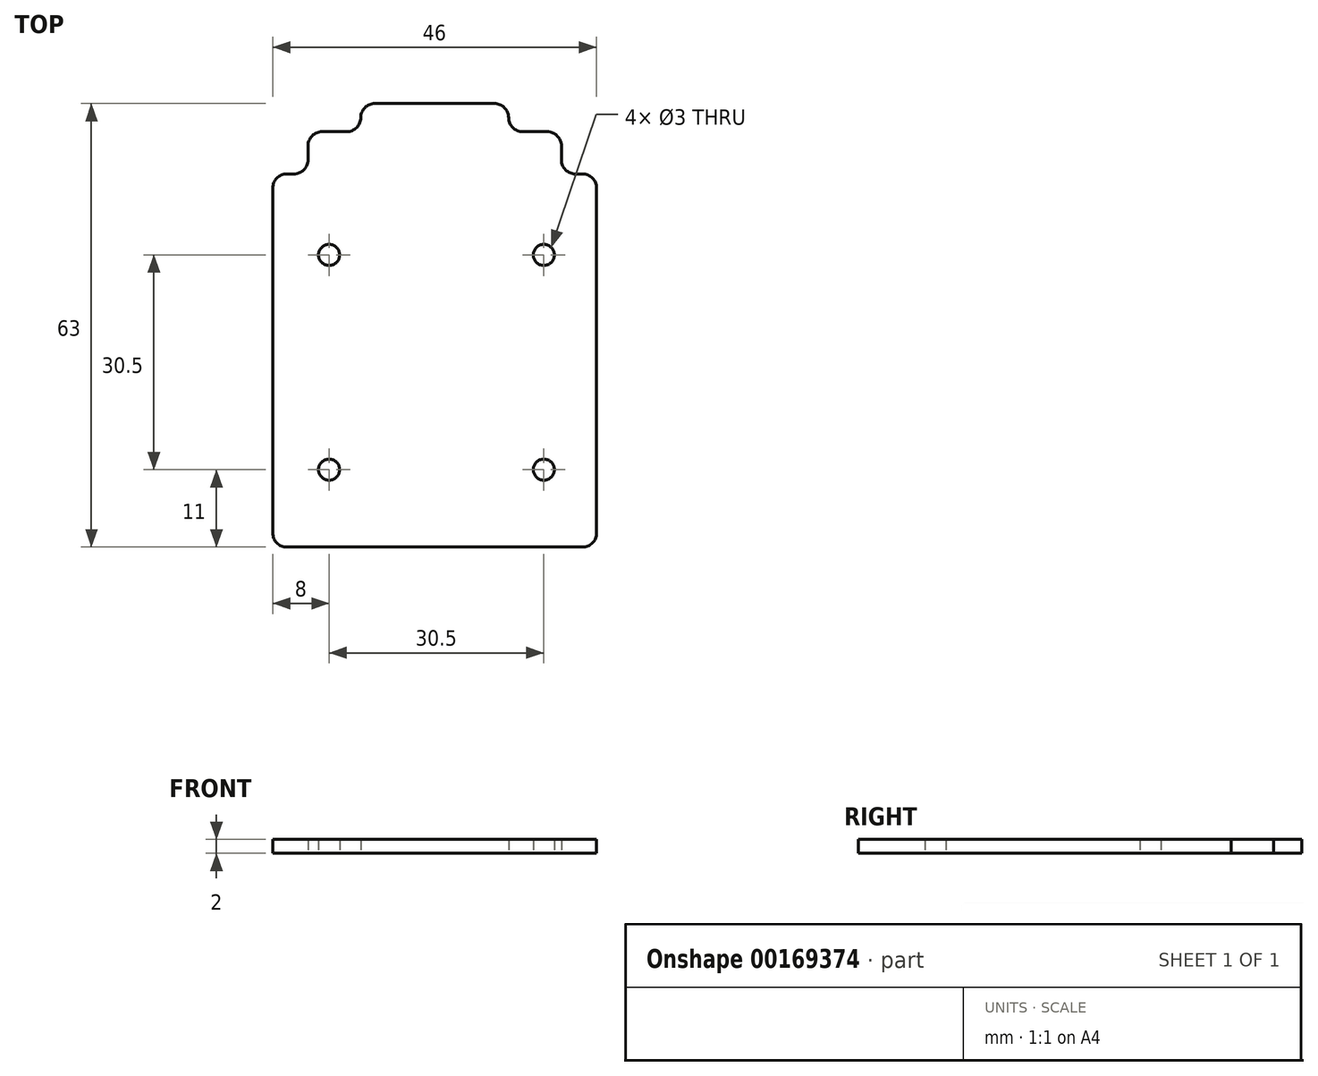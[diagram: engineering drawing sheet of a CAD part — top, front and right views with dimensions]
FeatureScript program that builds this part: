
annotation { "Feature Type Name" : "Feature", "Feature Type Description" : "" }
export const myFeature = defineFeature(function(context is Context, id is Id, definition is map)
    precondition{}
    {
        {
            var Q0;
            Q0=qCreatedBy(makeId("Top.planeOp"),FACE);
            var sketch = newSketch(context, id + "F0", { "sketchPlane" : qUnion([Q0])});
            skLineSegment(sketch, "E0.bottom", {"start": v(-10.5, 31.5) * mm, "end": v(10.5, 31.5) * mm});
            skLineSegment(sketch, "E0.top", {"start": v(-23, -31.5) * mm, "end": v(23, -31.5) * mm});
            skLineSegment(sketch, "E0.left", {"start": v(-23, 21.5) * mm, "end": v(-23, -31.5) * mm});
            skLineSegment(sketch, "E0.right", {"start": v(23, 21.5) * mm, "end": v(23, -31.5) * mm});
            skCircle(sketch, "E1", {"center": v(-15, -20.5) * mm, "radius": 1.5 * mm});
            skCircle(sketch, "E2.0.1.0", {"center": v(-15, 10) * mm, "radius": 1.5 * mm});
            skCircle(sketch, "E2.1.0.0", {"center": v(15.5, -20.5) * mm, "radius": 1.5 * mm});
            skCircle(sketch, "E2.1.1.0", {"center": v(15.5, 10) * mm, "radius": 1.5 * mm});
            skLineSegment(sketch, "E2.direction1", {"start": v(-15, -20.5) * mm, "end": v(15.5, -20.5) * mm, "construction": true});
            skLineSegment(sketch, "E2.direction2", {"start": v(-15, -20.5) * mm, "end": v(-15, 10) * mm, "construction": true});
            skLineSegment(sketch, "E3", {"start": v(23, 21.5) * mm, "end": v(18, 21.5) * mm});
            skLineSegment(sketch, "E4", {"start": v(18, 21.5) * mm, "end": v(18, 27.5) * mm});
            skLineSegment(sketch, "E5", {"start": v(18, 27.5) * mm, "end": v(10.5, 27.5) * mm});
            skLineSegment(sketch, "E6", {"start": v(10.5, 27.5) * mm, "end": v(10.5, 31.5) * mm});
            skLineSegment(sketch, "E7", {"start": v(-23, 21.5) * mm, "end": v(-18, 21.5) * mm});
            skLineSegment(sketch, "E8", {"start": v(-18, 21.5) * mm, "end": v(-18, 27.5) * mm});
            skLineSegment(sketch, "E9", {"start": v(-18, 27.5) * mm, "end": v(-10.5, 27.5) * mm});
            skLineSegment(sketch, "E10", {"start": v(-10.5, 27.5) * mm, "end": v(-10.5, 31.5) * mm});
            skSolve(sketch);
        }
        {
            var Q0;
            Q0 = qSketchRegion(id + "F0", true);
            extrude(context, id + "F1", {"entities" : qUnion([Q0]), "depth" : 2 * mm});
        }
        {
            var Q0;
            Q0=makeQuery(id+"F1.opExtrude","SWEPT_EDGE",EDGE,{"disambiguationData":[OSD([sQuery(id+"F0.wireOp",EDGE,"E0.bottom"),sQuery(id+"F0.wireOp",EDGE,"E6")])]});
            var Q1;
            Q1=makeQuery(id+"F1.opExtrude","SWEPT_EDGE",EDGE,{"disambiguationData":[OSD([sQuery(id+"F0.wireOp",EDGE,"E0.right"),sQuery(id+"F0.wireOp",EDGE,"E3")])]});
            var Q2;
            Q2=makeQuery(id+"F1.opExtrude","SWEPT_EDGE",EDGE,{"disambiguationData":[OSD([sQuery(id+"F0.wireOp",EDGE,"E4"),sQuery(id+"F0.wireOp",EDGE,"E5")])]});
            var Q3;
            Q3=makeQuery(id+"F1.opExtrude","SWEPT_EDGE",EDGE,{"disambiguationData":[OSD([sQuery(id+"F0.wireOp",EDGE,"E3"),sQuery(id+"F0.wireOp",EDGE,"E4")])]});
            var Q4;
            Q4=makeQuery(id+"F1.opExtrude","SWEPT_EDGE",EDGE,{"disambiguationData":[OSD([sQuery(id+"F0.wireOp",EDGE,"E5"),sQuery(id+"F0.wireOp",EDGE,"E6")])]});
            var Q5;
            Q5=makeQuery(id+"F1.opExtrude","SWEPT_EDGE",EDGE,{"disambiguationData":[OSD([sQuery(id+"F0.wireOp",EDGE,"E0.bottom"),sQuery(id+"F0.wireOp",EDGE,"E10")])]});
            var Q6;
            Q6=makeQuery(id+"F1.opExtrude","SWEPT_EDGE",EDGE,{"disambiguationData":[OSD([sQuery(id+"F0.wireOp",EDGE,"E9"),sQuery(id+"F0.wireOp",EDGE,"E10")])]});
            var Q7;
            Q7=makeQuery(id+"F1.opExtrude","SWEPT_EDGE",EDGE,{"disambiguationData":[OSD([sQuery(id+"F0.wireOp",EDGE,"E8"),sQuery(id+"F0.wireOp",EDGE,"E9")])]});
            var Q8;
            Q8=makeQuery(id+"F1.opExtrude","SWEPT_EDGE",EDGE,{"disambiguationData":[OSD([sQuery(id+"F0.wireOp",EDGE,"E7"),sQuery(id+"F0.wireOp",EDGE,"E8")])]});
            var Q9;
            Q9=makeQuery(id+"F1.opExtrude","SWEPT_EDGE",EDGE,{"disambiguationData":[OSD([sQuery(id+"F0.wireOp",EDGE,"E0.left"),sQuery(id+"F0.wireOp",EDGE,"E7")])]});
            var Q10;
            Q10=makeQuery(id+"F1.opExtrude","SWEPT_EDGE",EDGE,{"disambiguationData":[OSD([sQuery(id+"F0.wireOp",EDGE,"E0.top"),sQuery(id+"F0.wireOp",EDGE,"E0.left")])]});
            var Q11;
            Q11=makeQuery(id+"F1.opExtrude","SWEPT_EDGE",EDGE,{"disambiguationData":[OSD([sQuery(id+"F0.wireOp",EDGE,"E0.top"),sQuery(id+"F0.wireOp",EDGE,"E0.right")])]});
            fillet(context, id + "F2", {"entities" : qUnion([Q0, Q1, Q2, Q3, Q4, Q5, Q6, Q7, Q8, Q9, Q10, Q11]), "radius" : 2 * mm, "tangentPropagation" : true, "allowEdgeOverflow" : false});
        }
    });
